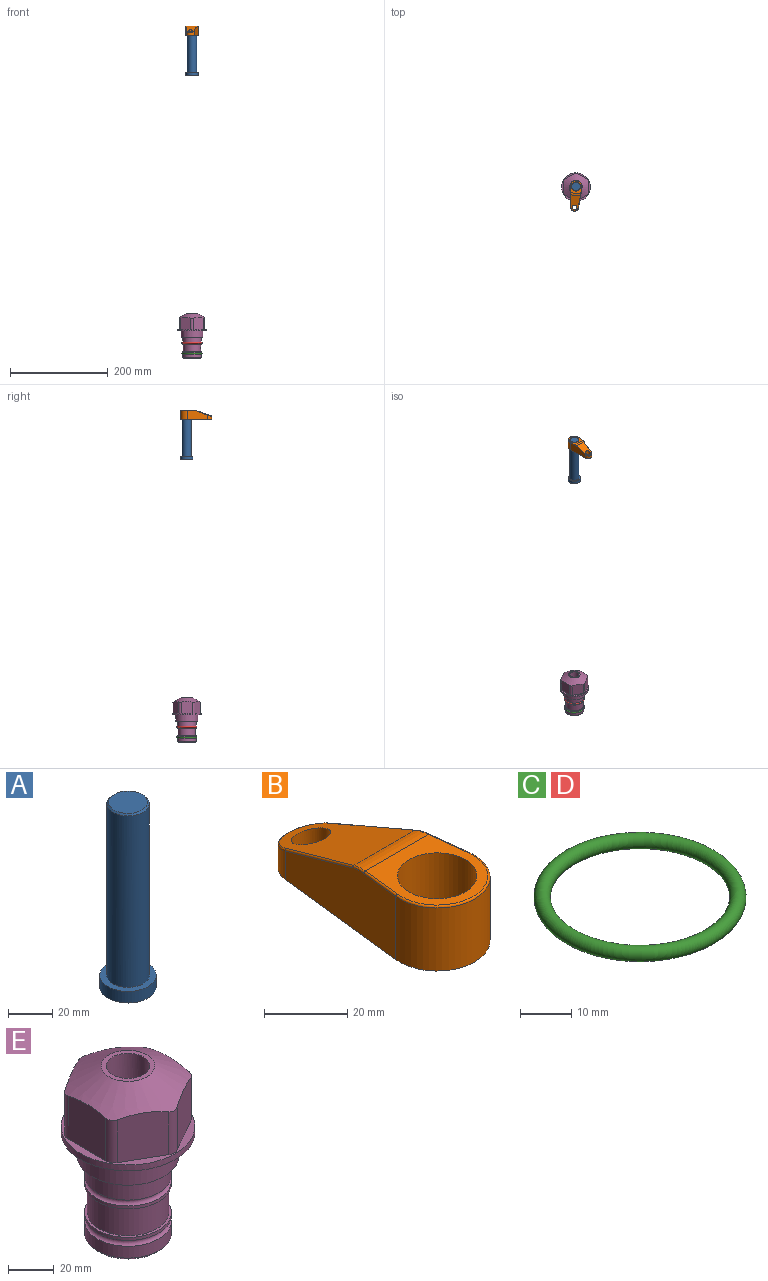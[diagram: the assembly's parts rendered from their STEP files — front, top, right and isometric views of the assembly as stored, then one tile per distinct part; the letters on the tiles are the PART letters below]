
ASSEMBLY  parts=5 mates=3
PART A: 6 faces, bbox 25.4x25.4x101.6 mm
  f0: plane 17.46x17.46mm, normal (0,0,1), area 239.5mm2, adj f5
  f1: plane 25.4x25.4mm, normal (0,0,-1), area 506.7mm2, adj f2
  f2: cylinder r=12.7mm len=25.4mm, axis (0,0,1), area 506.7mm2, adj f1,f3
  f3: plane 25.4x25.4mm, normal (0,0,1), area 221.7mm2, adj f2,f4
  f4: cylinder r=9.53mm len=94.46mm, axis (0,0,1), area 5653mm2, adj f3,f5
  f5: cone r=8.73mm half-angle=45deg, axis (0,0,-1), area 64.4mm2, adj f0,f4
PART B: 44 faces, bbox 27.5x64.5x19.1 mm
  f0: plane 2.3x0.95mm, normal (0,0,-1), area 1mm2, adj f25,f30,f34
  f1: plane 63.5x25.4mm, normal (0,0,-1), area 561.7mm2, adj f2,f3,f4,f5,f6,f7,f19,f20
  f2: cylinder r=12.7mm len=25.4mm, axis (0,0,-1), area 792.2mm2, adj f1,f3,f5,f13
  f3: plane 42.33x18.54mm, normal (0.99,0.11,0), area 647mm2, adj f1,f2,f4,f11,f12,f14
  f4: cylinder r=7.94mm len=15.78mm, axis (0,0,-1), area 158.6mm2, adj f1,f3,f5,f16
  f5: plane 42.33x18.54mm, normal (-0.99,0.11,0), area 647mm2, adj f1,f2,f4,f15,f17,f18
  f6: cylinder r=9.53mm len=19.05mm, axis (0,0,-1), area 1140.1mm2, adj f1,f8
  f7: cylinder r=4.76mm len=10.98mm, axis (0,0,-1), area 276.1mm2, adj f1,f9
  f8: plane 25.83x24.38mm, normal (0,0,1), area 262.2mm2, adj f6,f10,f11,f13,f15
  f9: plane 32.49x20.55mm, normal (0,0.34,0.94), area 489.9mm2, adj f7,f10,f14,f16,f18
  f10: cylinder r=12.7mm len=21.49mm, axis (-1,0,0), area 93.2mm2, adj f8,f9,f12,f17
  f11: cylinder r=0.51mm len=12.34mm, axis (0.11,-0.99,0), area 9.9mm2, adj f3,f8,f12,f13
  f12: bspline ~7.62x1.64mm, area 3.5mm2, adj f3,f10,f11,f14
  f13: torus R=12.19mm, axis (0,0,1), area 33.6mm2, adj f2,f8,f11,f15
  f14: cylinder r=0.51mm len=26.01mm, axis (0.1,-0.93,0.34), area 21.6mm2, adj f3,f9,f12,f16
  f15: cylinder r=0.51mm len=12.34mm, axis (0.11,0.99,0), area 9.9mm2, adj f5,f8,f13,f17
  f16: bspline ~15.78x7.05mm, area 15.7mm2, adj f4,f9,f14,f18
  f17: bspline ~7.62x1.64mm, area 3.5mm2, adj f5,f10,f15,f18
  f18: cylinder r=0.51mm len=26.01mm, axis (0.1,0.93,-0.34), area 21.6mm2, adj f5,f9,f16,f17
  f19: plane 21.6x14.29mm, normal (-0.99,-0.11,0), area 242.6mm2, adj f1,f26,f28,f34,f36,f38
  f20: plane 21.6x14.29mm, normal (0.99,-0.11,0), area 242.6mm2, adj f1,f27,f29,f37,f39,f41
  f21: cylinder r=12.7mm len=14.29mm, axis (0,0,-1), area 173.2mm2, adj f1,f26,f27,f30,f31,f33
  f22: cylinder r=7.94mm len=7.63mm, axis (0,0,-1), area 53.8mm2, adj f1,f28,f29,f42
  f23: plane 2.3x0.95mm, normal (0,0,-1), area 1mm2, adj f25,f33,f37
  f24: plane 17.94x12.32mm, normal (0,-0.34,-0.94), area 191.2mm2, adj f25,f38,f41,f42
  f25: cylinder r=9.53mm len=12.93mm, axis (-1,0,0), area 37.5mm2, adj f0,f23,f24,f31,f36,f39
  f26: cylinder r=1.59mm len=14.29mm, axis (0,0,-1), area 49mm2, adj f1,f19,f21,f32
  f27: cylinder r=1.59mm len=14.29mm, axis (0,0,-1), area 49mm2, adj f1,f20,f21,f35
  f28: cylinder r=1.59mm len=7.28mm, axis (0,0,-1), area 22.1mm2, adj f1,f19,f22,f40
  f29: cylinder r=1.59mm len=7.28mm, axis (0,0,-1), area 22.1mm2, adj f1,f20,f22,f43
  f30: torus R=14.29mm, axis (0,0,1), area 5.8mm2, adj f0,f21,f31,f32
  f31: bspline ~11.06x2.73mm, area 20.8mm2, adj f21,f25,f30,f33
  f32: sphere r=1.59mm, area 5.4mm2, adj f26,f30,f34
  f33: torus R=14.29mm, axis (0,0,1), area 5.8mm2, adj f21,f23,f31,f35
  f34: cylinder r=1.59mm len=1.68mm, axis (-0.11,0.99,0), area 2.4mm2, adj f0,f19,f32,f36
  f35: sphere r=1.59mm, area 5.4mm2, adj f27,f33,f37
  f36: bspline ~5.82x2.33mm, area 7.7mm2, adj f19,f25,f34,f38
  f37: cylinder r=1.59mm len=1.68mm, axis (0.11,0.99,0), area 2.4mm2, adj f20,f23,f35,f39
  f38: cylinder r=1.59mm len=18.33mm, axis (0.1,-0.93,0.34), area 46.7mm2, adj f19,f24,f36,f40
  f39: bspline ~5.82x2.33mm, area 7.7mm2, adj f20,f25,f37,f41
  f40: sphere r=1.59mm, area 3.6mm2, adj f28,f38,f42
  f41: cylinder r=1.59mm len=18.33mm, axis (0.1,0.93,-0.34), area 46.7mm2, adj f20,f24,f39,f43
  f42: bspline ~8.31x1.84mm, area 15.3mm2, adj f22,f24,f40,f43
  f43: sphere r=1.59mm, area 3.6mm2, adj f29,f41,f42
PART C: 1 faces, bbox 44.7x44.7x3.2 mm
  f0: torus R=19.05mm, axis (0,0,1), area 1193.9mm2
PART D: same geometry as C
PART E: 36 faces, bbox 58.7x58.7x91.2 mm
  f0: cylinder r=17.78mm len=35.56mm, axis (0,0,1), area 1670.8mm2, adj f23,f24,f31
  f1: cylinder r=19.05mm len=38.1mm, axis (0,0,1), area 1191.9mm2, adj f26,f27,f30
  f2: plane 58.66x58.66mm, normal (0,0,-1), area 1150.6mm2, adj f3,f28
  f3: cylinder r=29.33mm len=58.66mm, axis (0,0,-1), area 585.1mm2, adj f2,f4
  f4: plane 58.66x58.66mm, normal (0,0,1), area 475.9mm2, adj f3,f5,f6,f7,f8,f9,f10,f11
  f5: plane 24.5x20.32mm, normal (-0.5,0.87,0), area 562.8mm2, adj f4,f15,f16,f17
  f6: plane 24.5x20.32mm, normal (0.5,0.87,0), area 562.8mm2, adj f4,f14,f15,f17
  f7: plane 24.5x23.48mm, normal (1,0,0), area 562.8mm2, adj f4,f13,f14,f17
  f8: plane 24.5x20.32mm, normal (0.5,-0.87,0), area 562.8mm2, adj f4,f12,f13,f17
  f9: plane 24.5x20.32mm, normal (-0.5,-0.87,0), area 562.8mm2, adj f4,f11,f12,f17
  f10: plane 24.5x23.48mm, normal (-1,0,0), area 562.8mm2, adj f4,f11,f16,f17
  f11: cylinder r=5.08mm len=23.01mm, axis (0,0,-1), area 121.2mm2, adj f4,f9,f10,f17
  f12: cylinder r=5.08mm len=23.01mm, axis (0,0,-1), area 121.2mm2, adj f4,f8,f9,f17
  f13: cylinder r=5.08mm len=23.01mm, axis (0,0,-1), area 121.2mm2, adj f4,f7,f8,f17
  f14: cylinder r=5.08mm len=23.01mm, axis (0,0,-1), area 121.2mm2, adj f4,f6,f7,f17
  f15: cylinder r=5.08mm len=23.01mm, axis (0,0,-1), area 121.2mm2, adj f4,f5,f6,f17
  f16: cylinder r=5.08mm len=23.01mm, axis (0,0,-1), area 121.2mm2, adj f4,f5,f10,f17
  f17: cone r=11.73mm half-angle=60deg, axis (0,0,-1), area 2071.8mm2, adj f5,f6,f7,f8,f9,f10,f11,f12
  f18: plane 23.46x23.46mm, normal (0,0,1), area 147.4mm2, adj f17,f35
  f19: plane 34.93x34.93mm, normal (0,0,-1), area 958mm2, adj f29
  f20: cylinder r=19.05mm len=38.1mm, axis (0,0,1), area 760.1mm2, adj f21,f29
  f21: torus R=19.05mm, axis (0,0,1), area 565.3mm2, adj f20,f22
  f22: cylinder r=19.05mm len=38.1mm, axis (0,0,1), area 190mm2, adj f21,f23
  f23: plane 38.1x38.1mm, normal (0,0,1), area 146.9mm2, adj f0,f22
  f24: plane 38.1x38.1mm, normal (0,0,-1), area 146.9mm2, adj f0,f25
  f25: cylinder r=19.05mm len=38.1mm, axis (0,0,1), area 190mm2, adj f24,f26
  f26: torus R=19.05mm, axis (0,0,1), area 565.3mm2, adj f1,f25
  f27: plane 44.45x44.45mm, normal (0,0,-1), area 411.7mm2, adj f1,f28
  f28: cylinder r=22.23mm len=44.45mm, axis (0,0,1), area 1773.5mm2, adj f2,f27
  f29: cone r=19.05mm half-angle=45deg, axis (0,0,1), area 257.5mm2, adj f19,f20
  f30: cylinder r=3.17mm len=6.75mm, axis (-1,0,0), area 128mm2, adj f1,f33
  f31: cylinder r=3.17mm len=6.35mm, axis (-1,0,0), area 102.5mm2, adj f0,f33
  f32: plane 25.4x25.4mm, normal (0,0,1), area 506.7mm2, adj f33
  f33: cylinder r=12.7mm len=66.42mm, axis (0,0,-1), area 5236.2mm2, adj f30,f31,f32,f34
  f34: cone r=9.53mm half-angle=30deg, axis (0,0,-1), area 443.4mm2, adj f33,f35
  f35: cylinder r=9.53mm len=19.05mm, axis (0,0,-1), area 849mm2, adj f18,f34
PLACE A rot(axis=(0,0,-1),94deg) t=(0,0,551.06)mm
PLACE B rot(axis=(0,0,1),176deg) t=(0,0,605.67)mm
PLACE C t=(0,0,-21.59)mm
PLACE D at identity
PLACE E at identity fixed
MATE fastened C.f0 <-> E.f0  axis (0,0,1) through (0,0,-46.1)mm
MATE cylindrical A.f2 <-> E.f0  axis (0,0,1) through (0,0,576.7)mm
MATE fastened B.f2 <-> A.f2  axis (0,0,1) through (0,0,624.72)mm
